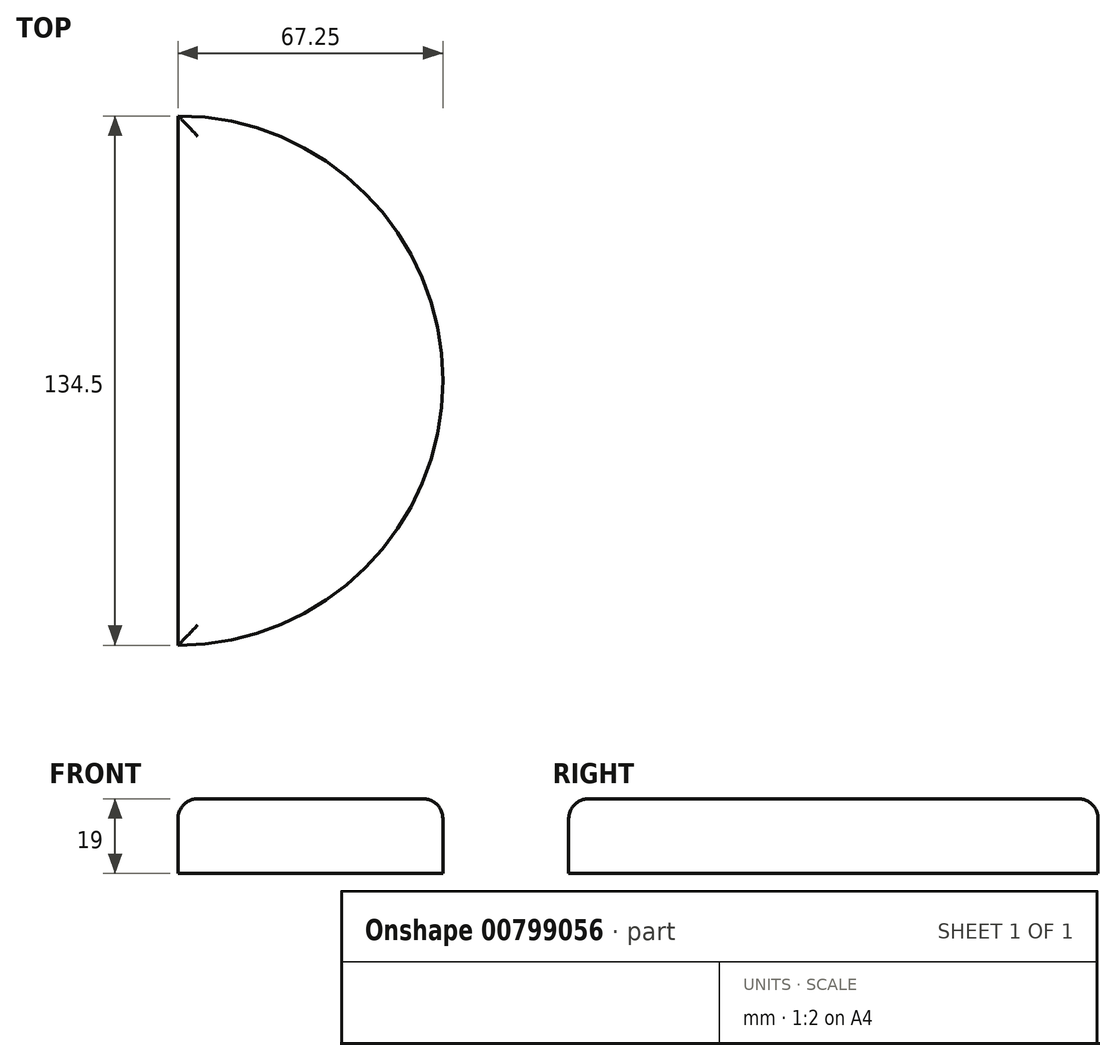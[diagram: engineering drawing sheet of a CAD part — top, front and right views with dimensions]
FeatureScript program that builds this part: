
annotation { "Feature Type Name" : "Feature", "Feature Type Description" : "" }
export const myFeature = defineFeature(function(context is Context, id is Id, definition is map)
    precondition{}
    {
        {
            var Q0;
            Q0=qCreatedBy(makeId("Top.planeOp"),FACE);
            var sketch = newSketch(context, id + "F0", { "sketchPlane" : qUnion([Q0])});
            skLineSegment(sketch, "E0", {"start": v(0, -67.25) * mm, "end": v(0, 67.25) * mm});
            skArc(sketch, "E1", {"start": v(0, 67.25) * mm, "mid": v(-67.25, 0) * mm, "end": v(0, -67.25) * mm});
            skArc(sketch, "E2", {"start": v(0, -67.25) * mm, "mid": v(67.25, 0) * mm, "end": v(0, 67.25) * mm});
            skSolve(sketch);
        }
        {
            var Q0;
            Q0=makeQuery(id+"F0.imprint","IMPRINT",FACE,{"disambiguationData":[TD([[makeQuery(id+"F0.imprint","IMPRINT",EDGE,{"derivedFrom":sQuery(id+"F0.wireOp",EDGE,"E0")}),-1.0]])]});
            extrude(context, id + "F1", {"entities" : qUnion([Q0]), "depth" : 19 * mm, "offsetDistance" : 25 * mm});
        }
        {
            var Q0;
            Q0=makeQuery(id+"F1.opExtrude","CAP_FACE",FACE,{"disambiguationData":[OSD([sQuery(id+"F0.wireOp",EDGE,"E0"),sQuery(id+"F0.wireOp",EDGE,"E2")])],"isStart":false});
            fillet(context, id + "F2", {"entities" : qUnion([Q0]), "radius" : 5 * mm, "tangentPropagation" : true, "allowEdgeOverflow" : false});
        }
    });
